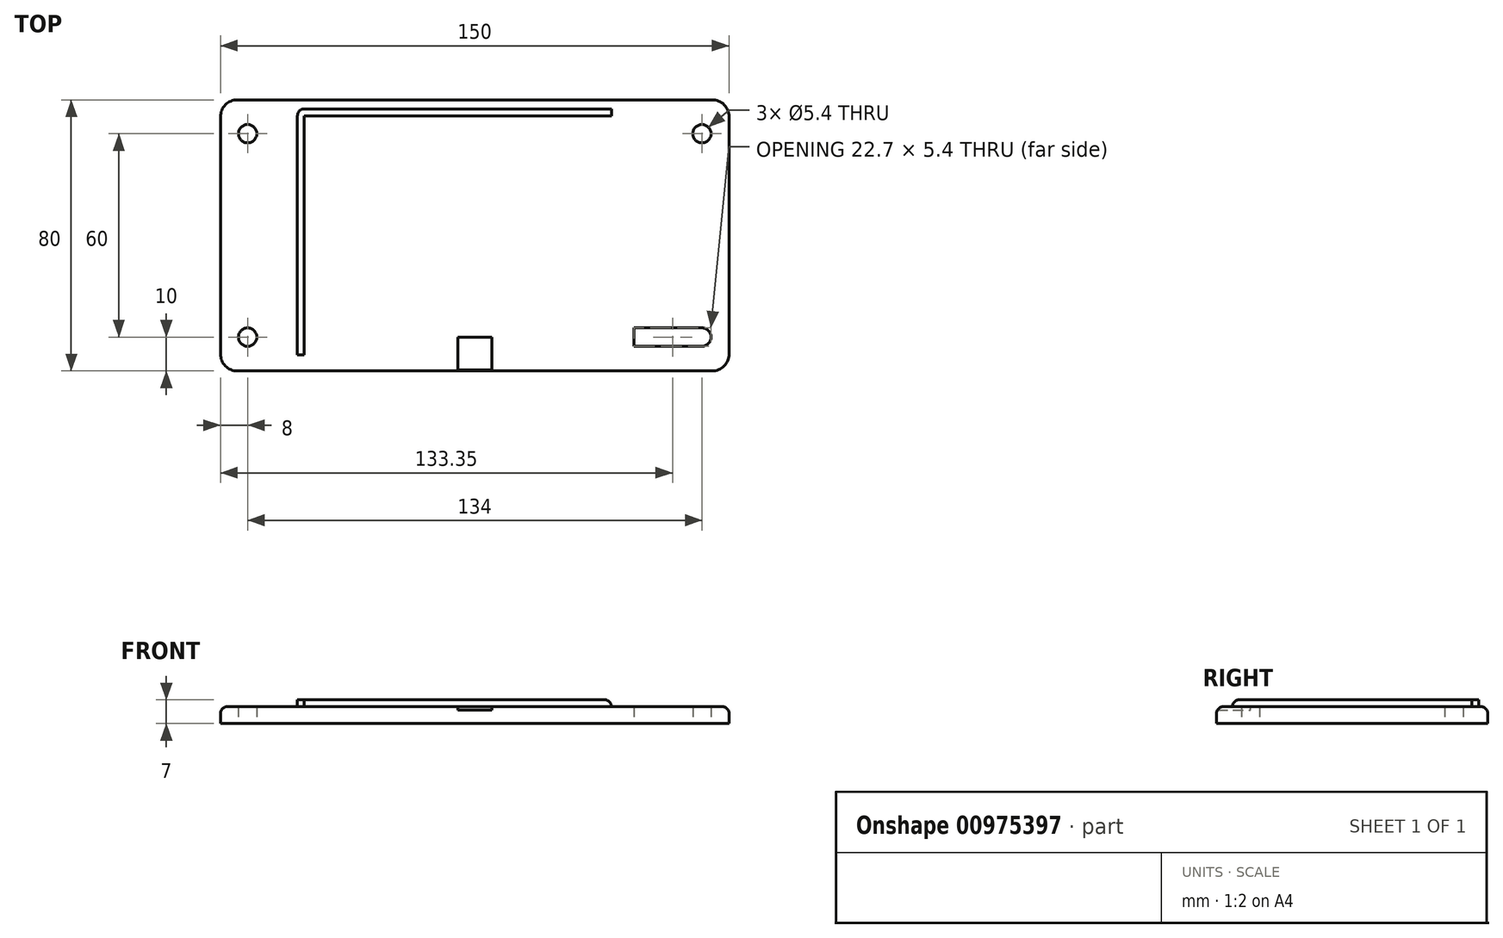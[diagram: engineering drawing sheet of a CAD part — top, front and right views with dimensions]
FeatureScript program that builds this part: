
annotation { "Feature Type Name" : "Feature", "Feature Type Description" : "" }
export const myFeature = defineFeature(function(context is Context, id is Id, definition is map)
    precondition{}
    {
        {
            var Q0;
            Q0=qCreatedBy(makeId("Top.planeOp"),FACE);
            var sketch = newSketch(context, id + "F0", { "sketchPlane" : qUnion([Q0])});
            skPoint(sketch, "E0.middle", {"position": v(0, 0) * mm});
            skLineSegment(sketch, "E1.bottom", {"start": v(-75, 40) * mm, "end": v(75, 40) * mm});
            skLineSegment(sketch, "E1.top", {"start": v(-75, -40) * mm, "end": v(75, -40) * mm});
            skLineSegment(sketch, "E1.left", {"start": v(-75, 40) * mm, "end": v(-75, -40) * mm});
            skLineSegment(sketch, "E1.right", {"start": v(75, 40) * mm, "end": v(75, -40) * mm});
            skLineSegment(sketch, "E2", {"start": v(-75, 0) * mm, "end": v(75, 0) * mm, "construction": true});
            skLineSegment(sketch, "E3", {"start": v(0, 40) * mm, "end": v(0, -40) * mm, "construction": true});
            skCircle(sketch, "E4", {"center": v(67, 30) * mm, "radius": 2.7 * mm});
            skCircle(sketch, "E5.MirrorC", {"center": v(67, -30) * mm, "radius": 2.7 * mm});
            skCircle(sketch, "E6.MirrorC", {"center": v(-67, 30) * mm, "radius": 2.7 * mm});
            skCircle(sketch, "E7.MirrorC", {"center": v(-67, -30) * mm, "radius": 2.7 * mm});
            skLineSegment(sketch, "E8.bottom", {"start": v(67, -27.3) * mm, "end": v(47, -27.3) * mm});
            skLineSegment(sketch, "E8.top", {"start": v(67, -32.7) * mm, "end": v(47, -32.7) * mm});
            skLineSegment(sketch, "E8.left", {"start": v(67, -27.3) * mm, "end": v(67, -32.7) * mm});
            skLineSegment(sketch, "E8.right", {"start": v(47, -27.3) * mm, "end": v(47, -32.7) * mm});
            skSolve(sketch);
        }
        {
            var Q0;
            Q0 = qSketchRegion(id + "F0", true);
            extrude(context, id + "F1", {"entities" : qUnion([Q0]), "depth" : 5 * mm, "offsetDistance" : 25 * mm});
        }
        {
            var Q0;
            Q0=makeQuery(id+"F1.opExtrude","CAP_FACE",FACE,{"disambiguationData":[OSD([sQuery(id+"F0.wireOp",EDGE,"E0.bottom"),sQuery(id+"F0.wireOp",EDGE,"E0.top"),sQuery(id+"F0.wireOp",EDGE,"E0.left"),sQuery(id+"F0.wireOp",EDGE,"E0.right"),sQuery(id+"F0.wireOp",EDGE,"E1.bottom"),sQuery(id+"F0.wireOp",EDGE,"E1.top"),sQuery(id+"F0.wireOp",EDGE,"E1.left"),sQuery(id+"F0.wireOp",EDGE,"E1.right")])],"isStart":false});
            var sketch = newSketch(context, id + "F2", { "sketchPlane" : qUnion([Q0])});
            skLineSegment(sketch, "E9.bottom", {"start": v(-50.3, 35.3) * mm, "end": v(50.3, 35.3) * mm});
            skLineSegment(sketch, "E9.top", {"start": v(-50.3, -35.3) * mm, "end": v(50.3, -35.3) * mm});
            skLineSegment(sketch, "E9.left", {"start": v(-50.3, 35.3) * mm, "end": v(-50.3, -35.3) * mm});
            skLineSegment(sketch, "E9.right", {"start": v(50.3, 35.3) * mm, "end": v(50.3, -35.3) * mm});
            skPoint(sketch, "E9.middle", {"position": v(0, 0) * mm});
            skLineSegment(sketch, "E10.bottom", {"start": v(-52.3, 37.3) * mm, "end": v(52.3, 37.3) * mm});
            skLineSegment(sketch, "E10.top", {"start": v(-52.3, -37.3) * mm, "end": v(52.3, -37.3) * mm});
            skLineSegment(sketch, "E10.left", {"start": v(-52.3, 37.3) * mm, "end": v(-52.3, -37.3) * mm});
            skLineSegment(sketch, "E10.right", {"start": v(52.3, 37.3) * mm, "end": v(52.3, -37.3) * mm});
            skLineSegment(sketch, "E11", {"start": v(0, 40) * mm, "end": v(0, -40) * mm, "construction": true});
            skLineSegment(sketch, "E12", {"start": v(-52.3, 40) * mm, "end": v(-50.3, 40) * mm});
            skLineSegment(sketch, "E13", {"start": v(-50.3, -35.3) * mm, "end": v(-52.3, -35.3) * mm});
            skLineSegment(sketch, "E14", {"start": v(40.3, 35.3) * mm, "end": v(40.3, 37.3) * mm});
            skSolve(sketch);
        }
        {
            var Q0;
            {var subQ4=sQuery(id+"F2.wireOp",EDGE,"E9.left");Q0=makeQuery(id+"F2.imprint","IMPRINT",FACE,{"disambiguationData":[TD([[makeQuery(id+"F2.imprint","IMPRINT",EDGE,{"derivedFrom":subQ4}),-1.0]])]});}
            extrude(context, id + "F3", {"entities" : qUnion([Q0]), "operationType" : NewBodyOperationType.ADD, "depth" : 2 * mm, "offsetDistance" : 25 * mm});
        }
        {
            var Q0;
            Q0=makeQuery(id+"F1.opExtrude","SWEPT_EDGE",EDGE,{"disambiguationData":[OSD([sQuery(id+"F0.wireOp",EDGE,"E1.top"),sQuery(id+"F0.wireOp",EDGE,"E1.right")])]});
            var Q1;
            Q1=makeQuery(id+"F1.opExtrude","SWEPT_EDGE",EDGE,{"disambiguationData":[OSD([sQuery(id+"F0.wireOp",EDGE,"E1.top"),sQuery(id+"F0.wireOp",EDGE,"E1.left")])]});
            var Q2;
            Q2=makeQuery(id+"F1.opExtrude","SWEPT_EDGE",EDGE,{"disambiguationData":[OSD([sQuery(id+"F0.wireOp",EDGE,"E1.bottom"),sQuery(id+"F0.wireOp",EDGE,"E1.left")])]});
            var Q3;
            Q3=makeQuery(id+"F1.opExtrude","SWEPT_EDGE",EDGE,{"disambiguationData":[OSD([sQuery(id+"F0.wireOp",EDGE,"E1.bottom"),sQuery(id+"F0.wireOp",EDGE,"E1.right")])]});
            fillet(context, id + "F4", {"entities" : qUnion([Q0, Q1, Q2, Q3]), "radius" : 5 * mm, "tangentPropagation" : true, "allowEdgeOverflow" : false});
        }
        {
            var Q0;
            Q0=makeQuery(id+"F3.opExtrude","CAP_EDGE",EDGE,{"disambiguationData":[OSD([sQuery(id+"F2.wireOp",EDGE,"E13")])],"isStart":false});
            var Q1;
            Q1=makeQuery(id+"F3.opExtrude","CAP_EDGE",EDGE,{"disambiguationData":[OSD([sQuery(id+"F2.wireOp",EDGE,"E14")])],"isStart":false});
            fillet(context, id + "F5", {"entities" : qUnion([Q0, Q1]), "radius" : 2 * mm, "tangentPropagation" : true, "allowEdgeOverflow" : false});
        }
        {
            var Q0;
            Q0=makeQuery(id+"F3.opExtrude","SWEPT_EDGE",EDGE,{"disambiguationData":[OSD([sQuery(id+"F2.wireOp",EDGE,"E10.bottom"),sQuery(id+"F2.wireOp",EDGE,"E10.left")])]});
            fillet(context, id + "F6", {"entities" : qUnion([Q0]), "radius" : 2 * mm, "tangentPropagation" : true, "allowEdgeOverflow" : false});
        }
        {
            var Q0;
            Q0=makeQuery(id+"F1.opExtrude","CAP_FACE",FACE,{"disambiguationData":[OSD([sQuery(id+"F0.wireOp",EDGE,"E0.bottom"),sQuery(id+"F0.wireOp",EDGE,"E0.top"),sQuery(id+"F0.wireOp",EDGE,"E0.left"),sQuery(id+"F0.wireOp",EDGE,"E0.right"),sQuery(id+"F0.wireOp",EDGE,"E1.bottom"),sQuery(id+"F0.wireOp",EDGE,"E1.top"),sQuery(id+"F0.wireOp",EDGE,"E1.left"),sQuery(id+"F0.wireOp",EDGE,"E1.right"),sQuery(id+"F0.wireOp",EDGE,"E4"),sQuery(id+"F0.wireOp",EDGE,"E5.MirrorC"),sQuery(id+"F0.wireOp",EDGE,"E6.MirrorC"),sQuery(id+"F0.wireOp",EDGE,"E7.MirrorC")])],"isStart":false});
            var sketch = newSketch(context, id + "F7", { "sketchPlane" : qUnion([Q0])});
            skPoint(sketch, "E15.middle", {"position": v(0, -40) * mm});
            skLineSegment(sketch, "E16.bottom", {"start": v(5, -40) * mm, "end": v(-5, -40) * mm});
            skLineSegment(sketch, "E16.top", {"start": v(5, -30) * mm, "end": v(-5, -30) * mm});
            skLineSegment(sketch, "E16.left", {"start": v(5, -40) * mm, "end": v(5, -30) * mm});
            skLineSegment(sketch, "E16.right", {"start": v(-5, -40) * mm, "end": v(-5, -30) * mm});
            skSolve(sketch);
        }
        {
            var Q0;
            {var subQ0=sQuery(id+"F7.wireOp",EDGE,"E15.bottom");Q0=makeQuery(id+"F7.imprint","IMPRINT",FACE,{"disambiguationData":[TD([[makeQuery(id+"F7.imprint","IMPRINT",EDGE,{"derivedFrom":subQ0}),-1.0]])]});}
            var Q1;
            Q1=makeQuery(id+"F7.imprint","IMPRINT",FACE,{"disambiguationData":[TD([[makeQuery(id+"F7.imprint","IMPRINT",EDGE,{"derivedFrom":sQuery(id+"F7.wireOp",EDGE,"E16.bottom")}),1.0]])]});
            extrude(context, id + "F8", {"entities" : qUnion([Q0, Q1]), "operationType" : NewBodyOperationType.REMOVE, "oppositeDirection" : true, "depth" : 1 * mm, "offsetDistance" : 25 * mm});
        }
        {
            var Q0;
            {var subQ1=sQuery(id+"F0.wireOp",EDGE,"E1.top");Q0=makeQuery(id+"F8.boolean.opBoolean","SPLIT",EDGE,{"disambiguationData":[TD([makeQuery(id+"F8.opExtrude","SWEPT_FACE",FACE,{"disambiguationData":[OSD([sQuery(id+"F7.wireOp",EDGE,"E15.left")])]})])],"derivedFrom":makeQuery(id+"F1.opExtrude","CAP_EDGE",EDGE,{"disambiguationData":[OSD([subQ1])],"isStart":false})});}
            var Q1;
            {var subQ1=sQuery(id+"F0.wireOp",EDGE,"E1.top");Q1=makeQuery(id+"F8.boolean.opBoolean","SPLIT",EDGE,{"disambiguationData":[TD([makeQuery(id+"F8.opExtrude","SWEPT_FACE",FACE,{"disambiguationData":[OSD([sQuery(id+"F7.wireOp",EDGE,"E15.right")])]})])],"derivedFrom":makeQuery(id+"F1.opExtrude","CAP_EDGE",EDGE,{"disambiguationData":[OSD([subQ1])],"isStart":false})});}
            var Q2;
            {var subQ0=sQuery(id+"F0.wireOp",EDGE,"E1.left");var subQ1=sQuery(id+"F0.wireOp",EDGE,"E1.top");Q2=makeQuery(id+"F4.opFillet","BLEND_EDGE",EDGE,{"blendedFrom":[makeQuery(id+"F1.opExtrude","SWEPT_EDGE",EDGE,{"disambiguationData":[OSD([subQ1,subQ0])]}),makeQuery(id+"F1.opExtrude","CAP_FACE",FACE,{"disambiguationData":[OSD([sQuery(id+"F0.wireOp",EDGE,"E0.bottom"),sQuery(id+"F0.wireOp",EDGE,"E0.top"),sQuery(id+"F0.wireOp",EDGE,"E0.left"),sQuery(id+"F0.wireOp",EDGE,"E0.right"),sQuery(id+"F0.wireOp",EDGE,"E1.bottom"),subQ1,subQ0,sQuery(id+"F0.wireOp",EDGE,"E1.right"),sQuery(id+"F0.wireOp",EDGE,"E4"),sQuery(id+"F0.wireOp",EDGE,"E5.MirrorC"),sQuery(id+"F0.wireOp",EDGE,"E6.MirrorC"),sQuery(id+"F0.wireOp",EDGE,"E7.MirrorC")])],"isStart":false})],"blendedInto":[makeQuery(id+"F1.opExtrude","CAP_FACE",FACE,{"disambiguationData":[OSD([sQuery(id+"F0.wireOp",EDGE,"E0.bottom"),sQuery(id+"F0.wireOp",EDGE,"E0.top"),sQuery(id+"F0.wireOp",EDGE,"E0.left"),sQuery(id+"F0.wireOp",EDGE,"E0.right"),sQuery(id+"F0.wireOp",EDGE,"E1.bottom"),subQ1,subQ0,sQuery(id+"F0.wireOp",EDGE,"E1.right"),sQuery(id+"F0.wireOp",EDGE,"E4"),sQuery(id+"F0.wireOp",EDGE,"E5.MirrorC"),sQuery(id+"F0.wireOp",EDGE,"E6.MirrorC"),sQuery(id+"F0.wireOp",EDGE,"E7.MirrorC")])],"isStart":false})]});}
            var Q3;
            Q3=makeQuery(id+"F1.opExtrude","CAP_EDGE",EDGE,{"disambiguationData":[OSD([sQuery(id+"F0.wireOp",EDGE,"E1.left")])],"isStart":false});
            var Q4;
            Q4=makeQuery(id+"F1.opExtrude","CAP_EDGE",EDGE,{"disambiguationData":[OSD([sQuery(id+"F0.wireOp",EDGE,"E1.right")])],"isStart":false});
            var Q5;
            {var subQ0=sQuery(id+"F0.wireOp",EDGE,"E1.right");var subQ1=sQuery(id+"F0.wireOp",EDGE,"E1.top");Q5=makeQuery(id+"F4.opFillet","BLEND_EDGE",EDGE,{"blendedFrom":[makeQuery(id+"F1.opExtrude","SWEPT_EDGE",EDGE,{"disambiguationData":[OSD([subQ1,subQ0])]}),makeQuery(id+"F1.opExtrude","CAP_FACE",FACE,{"disambiguationData":[OSD([sQuery(id+"F0.wireOp",EDGE,"E0.bottom"),sQuery(id+"F0.wireOp",EDGE,"E0.top"),sQuery(id+"F0.wireOp",EDGE,"E0.left"),sQuery(id+"F0.wireOp",EDGE,"E0.right"),sQuery(id+"F0.wireOp",EDGE,"E1.bottom"),subQ1,sQuery(id+"F0.wireOp",EDGE,"E1.left"),subQ0,sQuery(id+"F0.wireOp",EDGE,"E4"),sQuery(id+"F0.wireOp",EDGE,"E5.MirrorC"),sQuery(id+"F0.wireOp",EDGE,"E6.MirrorC"),sQuery(id+"F0.wireOp",EDGE,"E7.MirrorC")])],"isStart":false})],"blendedInto":[makeQuery(id+"F1.opExtrude","CAP_FACE",FACE,{"disambiguationData":[OSD([sQuery(id+"F0.wireOp",EDGE,"E0.bottom"),sQuery(id+"F0.wireOp",EDGE,"E0.top"),sQuery(id+"F0.wireOp",EDGE,"E0.left"),sQuery(id+"F0.wireOp",EDGE,"E0.right"),sQuery(id+"F0.wireOp",EDGE,"E1.bottom"),subQ1,sQuery(id+"F0.wireOp",EDGE,"E1.left"),subQ0,sQuery(id+"F0.wireOp",EDGE,"E4"),sQuery(id+"F0.wireOp",EDGE,"E5.MirrorC"),sQuery(id+"F0.wireOp",EDGE,"E6.MirrorC"),sQuery(id+"F0.wireOp",EDGE,"E7.MirrorC")])],"isStart":false})]});}
            var Q6;
            {var subQ0=sQuery(id+"F0.wireOp",EDGE,"E1.right");var subQ1=sQuery(id+"F0.wireOp",EDGE,"E1.bottom");Q6=makeQuery(id+"F4.opFillet","BLEND_EDGE",EDGE,{"blendedFrom":[makeQuery(id+"F1.opExtrude","SWEPT_EDGE",EDGE,{"disambiguationData":[OSD([subQ1,subQ0])]}),makeQuery(id+"F1.opExtrude","CAP_FACE",FACE,{"disambiguationData":[OSD([sQuery(id+"F0.wireOp",EDGE,"E0.bottom"),sQuery(id+"F0.wireOp",EDGE,"E0.top"),sQuery(id+"F0.wireOp",EDGE,"E0.left"),sQuery(id+"F0.wireOp",EDGE,"E0.right"),subQ1,sQuery(id+"F0.wireOp",EDGE,"E1.top"),sQuery(id+"F0.wireOp",EDGE,"E1.left"),subQ0,sQuery(id+"F0.wireOp",EDGE,"E4"),sQuery(id+"F0.wireOp",EDGE,"E5.MirrorC"),sQuery(id+"F0.wireOp",EDGE,"E6.MirrorC"),sQuery(id+"F0.wireOp",EDGE,"E7.MirrorC")])],"isStart":false})],"blendedInto":[makeQuery(id+"F1.opExtrude","CAP_FACE",FACE,{"disambiguationData":[OSD([sQuery(id+"F0.wireOp",EDGE,"E0.bottom"),sQuery(id+"F0.wireOp",EDGE,"E0.top"),sQuery(id+"F0.wireOp",EDGE,"E0.left"),sQuery(id+"F0.wireOp",EDGE,"E0.right"),subQ1,sQuery(id+"F0.wireOp",EDGE,"E1.top"),sQuery(id+"F0.wireOp",EDGE,"E1.left"),subQ0,sQuery(id+"F0.wireOp",EDGE,"E4"),sQuery(id+"F0.wireOp",EDGE,"E5.MirrorC"),sQuery(id+"F0.wireOp",EDGE,"E6.MirrorC"),sQuery(id+"F0.wireOp",EDGE,"E7.MirrorC")])],"isStart":false})]});}
            var Q7;
            Q7=makeQuery(id+"F1.opExtrude","CAP_EDGE",EDGE,{"disambiguationData":[OSD([sQuery(id+"F0.wireOp",EDGE,"E1.bottom")])],"isStart":false});
            var Q8;
            {var subQ0=sQuery(id+"F0.wireOp",EDGE,"E1.left");var subQ1=sQuery(id+"F0.wireOp",EDGE,"E1.bottom");Q8=makeQuery(id+"F4.opFillet","BLEND_EDGE",EDGE,{"blendedFrom":[makeQuery(id+"F1.opExtrude","SWEPT_EDGE",EDGE,{"disambiguationData":[OSD([subQ1,subQ0])]}),makeQuery(id+"F1.opExtrude","CAP_FACE",FACE,{"disambiguationData":[OSD([sQuery(id+"F0.wireOp",EDGE,"E0.bottom"),sQuery(id+"F0.wireOp",EDGE,"E0.top"),sQuery(id+"F0.wireOp",EDGE,"E0.left"),sQuery(id+"F0.wireOp",EDGE,"E0.right"),subQ1,sQuery(id+"F0.wireOp",EDGE,"E1.top"),subQ0,sQuery(id+"F0.wireOp",EDGE,"E1.right"),sQuery(id+"F0.wireOp",EDGE,"E4"),sQuery(id+"F0.wireOp",EDGE,"E5.MirrorC"),sQuery(id+"F0.wireOp",EDGE,"E6.MirrorC"),sQuery(id+"F0.wireOp",EDGE,"E7.MirrorC")])],"isStart":false})],"blendedInto":[makeQuery(id+"F1.opExtrude","CAP_FACE",FACE,{"disambiguationData":[OSD([sQuery(id+"F0.wireOp",EDGE,"E0.bottom"),sQuery(id+"F0.wireOp",EDGE,"E0.top"),sQuery(id+"F0.wireOp",EDGE,"E0.left"),sQuery(id+"F0.wireOp",EDGE,"E0.right"),subQ1,sQuery(id+"F0.wireOp",EDGE,"E1.top"),subQ0,sQuery(id+"F0.wireOp",EDGE,"E1.right"),sQuery(id+"F0.wireOp",EDGE,"E4"),sQuery(id+"F0.wireOp",EDGE,"E5.MirrorC"),sQuery(id+"F0.wireOp",EDGE,"E6.MirrorC"),sQuery(id+"F0.wireOp",EDGE,"E7.MirrorC")])],"isStart":false})]});}
            fillet(context, id + "F9", {"entities" : qUnion([Q0, Q1, Q2, Q3, Q4, Q5, Q6, Q7, Q8]), "radius" : 2 * mm, "tangentPropagation" : true, "allowEdgeOverflow" : false});
        }
    });
